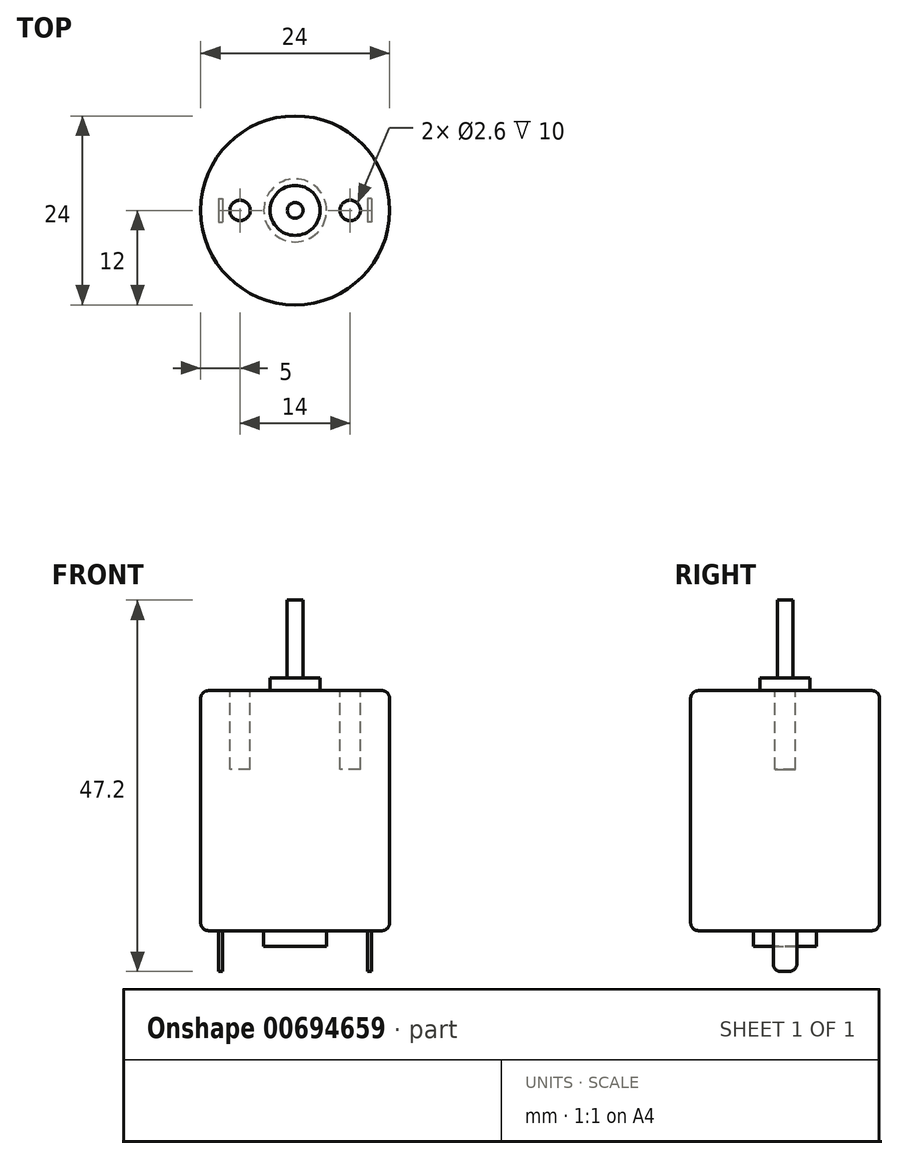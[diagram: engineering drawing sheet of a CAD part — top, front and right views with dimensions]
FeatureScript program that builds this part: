
annotation { "Feature Type Name" : "Feature", "Feature Type Description" : "" }
export const myFeature = defineFeature(function(context is Context, id is Id, definition is map)
    precondition{}
    {
        {
            var Q0;
            Q0=qCreatedBy(makeId("Top.planeOp"),FACE);
            var sketch = newSketch(context, id + "F0", { "sketchPlane" : qUnion([Q0])});
            skCircle(sketch, "E0", {"center": v(0, 0) * mm, "radius": 12 * mm});
            skSolve(sketch);
        }
        {
            var Q0;
            Q0=makeQuery(id+"F0.imprint","IMPRINT",FACE,{"disambiguationData":[TD([[makeQuery(id+"F0.imprint","IMPRINT",EDGE,{"derivedFrom":sQuery(id+"F0.wireOp",EDGE,"E0")}),1.0]])]});
            extrude(context, id + "F1", {"entities" : qUnion([Q0]), "depth" : 30.5 * mm});
        }
        {
            var Q0;
            Q0=makeQuery(id+"F1.opExtrude","CAP_FACE",FACE,{"disambiguationData":[OSD([sQuery(id+"F0.wireOp",EDGE,"E0")])],"isStart":false});
            var sketch = newSketch(context, id + "F2", { "sketchPlane" : qUnion([Q0])});
            skCircle(sketch, "E1", {"center": v(0, 0) * mm, "radius": 1 * mm});
            skSolve(sketch);
        }
        {
            var Q0;
            Q0=qSketchRegion(id+"F2",true);
            extrude(context, id + "F3", {"entities" : qUnion([Q0]), "operationType" : NewBodyOperationType.ADD, "depth" : 11.5 * mm});
        }
        {
            var Q0;
            Q0=makeQuery(id+"F1.opExtrude","CAP_FACE",FACE,{"disambiguationData":[OSD([sQuery(id+"F0.wireOp",EDGE,"E0")])],"isStart":false});
            var sketch = newSketch(context, id + "F4", { "sketchPlane" : qUnion([Q0])});
            skCircle(sketch, "E2", {"center": v(0, 0) * mm, "radius": 3.17 * mm});
            skSolve(sketch);
        }
        {
            var Q0;
            Q0=qSketchRegion(id+"F4",true);
            extrude(context, id + "F5", {"entities" : qUnion([Q0]), "operationType" : NewBodyOperationType.ADD, "depth" : 1.6 * mm});
        }
        {
            var Q0;
            Q0=makeQuery(id+"F1.opExtrude","CAP_FACE",FACE,{"disambiguationData":[OSD([sQuery(id+"F0.wireOp",EDGE,"E0")])],"isStart":false});
            var sketch = newSketch(context, id + "F6", { "sketchPlane" : qUnion([Q0])});
            skLineSegment(sketch, "E3", {"start": v(-12, 0) * mm, "end": v(12, 0) * mm, "construction": true});
            skCircle(sketch, "E4", {"center": v(7, 0) * mm, "radius": 1.3 * mm});
            skCircle(sketch, "E5", {"center": v(-7, 0) * mm, "radius": 1.3 * mm});
            skLineSegment(sketch, "E6", {"start": v(0, -12) * mm, "end": v(0, 12) * mm, "construction": true});
            skSolve(sketch);
        }
        {
            var Q0;
            Q0=makeQuery(id+"F6.imprint","IMPRINT",FACE,{"disambiguationData":[TD([[makeQuery(id+"F6.imprint","IMPRINT",EDGE,{"derivedFrom":sQuery(id+"F6.wireOp",EDGE,"E5")}),1.0]])]});
            var Q1;
            Q1=makeQuery(id+"F6.imprint","IMPRINT",FACE,{"disambiguationData":[TD([[makeQuery(id+"F6.imprint","IMPRINT",EDGE,{"derivedFrom":sQuery(id+"F6.wireOp",EDGE,"E4")}),1.0]])]});
            extrude(context, id + "F7", {"entities" : qUnion([Q0, Q1]), "operationType" : NewBodyOperationType.REMOVE, "oppositeDirection" : true, "depth" : 10 * mm});
        }
        {
            var Q0;
            Q0=makeQuery(id+"F1.opExtrude","CAP_FACE",FACE,{"disambiguationData":[OSD([sQuery(id+"F0.wireOp",EDGE,"E0")])],"isStart":true});
            var sketch = newSketch(context, id + "F8", { "sketchPlane" : qUnion([Q0])});
            skCircle(sketch, "E7", {"center": v(0, 0) * mm, "radius": 4 * mm});
            skSolve(sketch);
        }
        {
            var Q0;
            Q0=makeQuery(id+"F8.imprint","IMPRINT",FACE,{"disambiguationData":[TD([[makeQuery(id+"F8.imprint","IMPRINT",EDGE,{"derivedFrom":sQuery(id+"F8.wireOp",EDGE,"E7")}),1.0]])]});
            extrude(context, id + "F9", {"entities" : qUnion([Q0]), "operationType" : NewBodyOperationType.ADD, "depth" : 2 * mm});
        }
        {
            var Q0;
            Q0=makeQuery(id+"F1.opExtrude","CAP_FACE",FACE,{"disambiguationData":[OSD([sQuery(id+"F0.wireOp",EDGE,"E0")])],"isStart":true});
            var sketch = newSketch(context, id + "F10", { "sketchPlane" : qUnion([Q0])});
            skLineSegment(sketch, "E8.bottom", {"start": v(-9.7, -1.5) * mm, "end": v(-9.2, -1.5) * mm});
            skLineSegment(sketch, "E8.top", {"start": v(-9.7, 1.5) * mm, "end": v(-9.2, 1.5) * mm});
            skLineSegment(sketch, "E8.left", {"start": v(-9.7, -1.5) * mm, "end": v(-9.7, 1.5) * mm});
            skLineSegment(sketch, "E8.right", {"start": v(-9.2, -1.5) * mm, "end": v(-9.2, 1.5) * mm});
            skLineSegment(sketch, "E9", {"start": v(0, 12) * mm, "end": v(0, -12) * mm, "construction": true});
            skLineSegment(sketch, "E10", {"start": v(12, 0) * mm, "end": v(-12, 0) * mm, "construction": true});
            skLineSegment(sketch, "E11.bottom", {"start": v(9.7, -1.5) * mm, "end": v(9.2, -1.5) * mm});
            skLineSegment(sketch, "E11.top", {"start": v(9.7, 1.5) * mm, "end": v(9.2, 1.5) * mm});
            skLineSegment(sketch, "E11.left", {"start": v(9.7, -1.5) * mm, "end": v(9.7, 1.5) * mm});
            skLineSegment(sketch, "E11.right", {"start": v(9.2, -1.5) * mm, "end": v(9.2, 1.5) * mm});
            skSolve(sketch);
        }
        {
            var Q0;
            Q0=makeQuery(id+"F10.imprint","IMPRINT",FACE,{"disambiguationData":[TD([[makeQuery(id+"F10.imprint","IMPRINT",EDGE,{"derivedFrom":sQuery(id+"F10.wireOp",EDGE,"E8.bottom")}),1.0]])]});
            var Q1;
            Q1=makeQuery(id+"F10.imprint","IMPRINT",FACE,{"disambiguationData":[TD([[makeQuery(id+"F10.imprint","IMPRINT",EDGE,{"derivedFrom":sQuery(id+"F10.wireOp",EDGE,"E11.bottom")}),-1.0]])]});
            extrude(context, id + "F11", {"entities" : qUnion([Q0, Q1]), "operationType" : NewBodyOperationType.ADD, "depth" : 5.2 * mm});
        }
        {
            var Q0;
            Q0=makeQuery(id+"F11.opExtrude","CAP_EDGE",EDGE,{"disambiguationData":[OSD([sQuery(id+"F10.wireOp",EDGE,"E8.bottom")])],"isStart":false});
            var Q1;
            Q1=makeQuery(id+"F11.opExtrude","CAP_EDGE",EDGE,{"disambiguationData":[OSD([sQuery(id+"F10.wireOp",EDGE,"E8.top")])],"isStart":false});
            var Q2;
            Q2=makeQuery(id+"F11.opExtrude","CAP_EDGE",EDGE,{"disambiguationData":[OSD([sQuery(id+"F10.wireOp",EDGE,"E11.bottom")])],"isStart":false});
            var Q3;
            Q3=makeQuery(id+"F11.opExtrude","CAP_EDGE",EDGE,{"disambiguationData":[OSD([sQuery(id+"F10.wireOp",EDGE,"E11.top")])],"isStart":false});
            fillet(context, id + "F12", {"entities" : qUnion([Q0, Q1, Q2, Q3]), "radius" : 1 * mm, "tangentPropagation" : true, "allowEdgeOverflow" : false});
        }
        {
            var Q0;
            Q0=makeQuery(id+"F1.opExtrude","CAP_EDGE",EDGE,{"disambiguationData":[OSD([sQuery(id+"F0.wireOp",EDGE,"E0")])],"isStart":true});
            fillet(context, id + "F13", {"entities" : qUnion([Q0]), "radius" : 1 * mm, "tangentPropagation" : true, "allowEdgeOverflow" : false});
        }
        {
            var Q0;
            Q0=makeQuery(id+"F1.opExtrude","CAP_EDGE",EDGE,{"disambiguationData":[OSD([sQuery(id+"F0.wireOp",EDGE,"E0")])],"isStart":false});
            fillet(context, id + "F14", {"entities" : qUnion([Q0]), "radius" : 1 * mm, "tangentPropagation" : true, "allowEdgeOverflow" : false});
        }
    });
